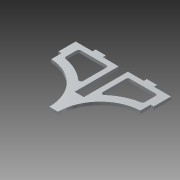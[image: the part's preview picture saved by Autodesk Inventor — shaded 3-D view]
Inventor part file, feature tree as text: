
AUTODESK INVENTOR PART (.ipt)
format: ipt  version: 2015 (Build 190159000, 159)  size: 157,696 bytes
history: native  units: mm
features: extrude x1, sketch x1
ambient origin geometry x8: Origin, YZ Plane, XZ Plane, XY Plane, X Axis, Y Axis, Z Axis, Center Point
bodies: Body1 (feature_tree)
feature tree (2):
  extrude  "Extrusion6"  Depth=3.0mm
  sketch  "Sketch1"  dims[d1=46.5mm d3=3.0mm d5=82.5mm d7=45.5mm d10=10.0mm d12=65.0mm d23=3.0mm d24=10.0mm d25=20.0mm d31=8.0mm d32=8.0mm d33=5.0mm d36=15.5mm d37=16.5mm d38=16.75mm d39=5.0mm d40=2.0mm d45=8.0mm d49=68.0mm d50=25.0mm d55=3.0mm d56=0.0mm]
